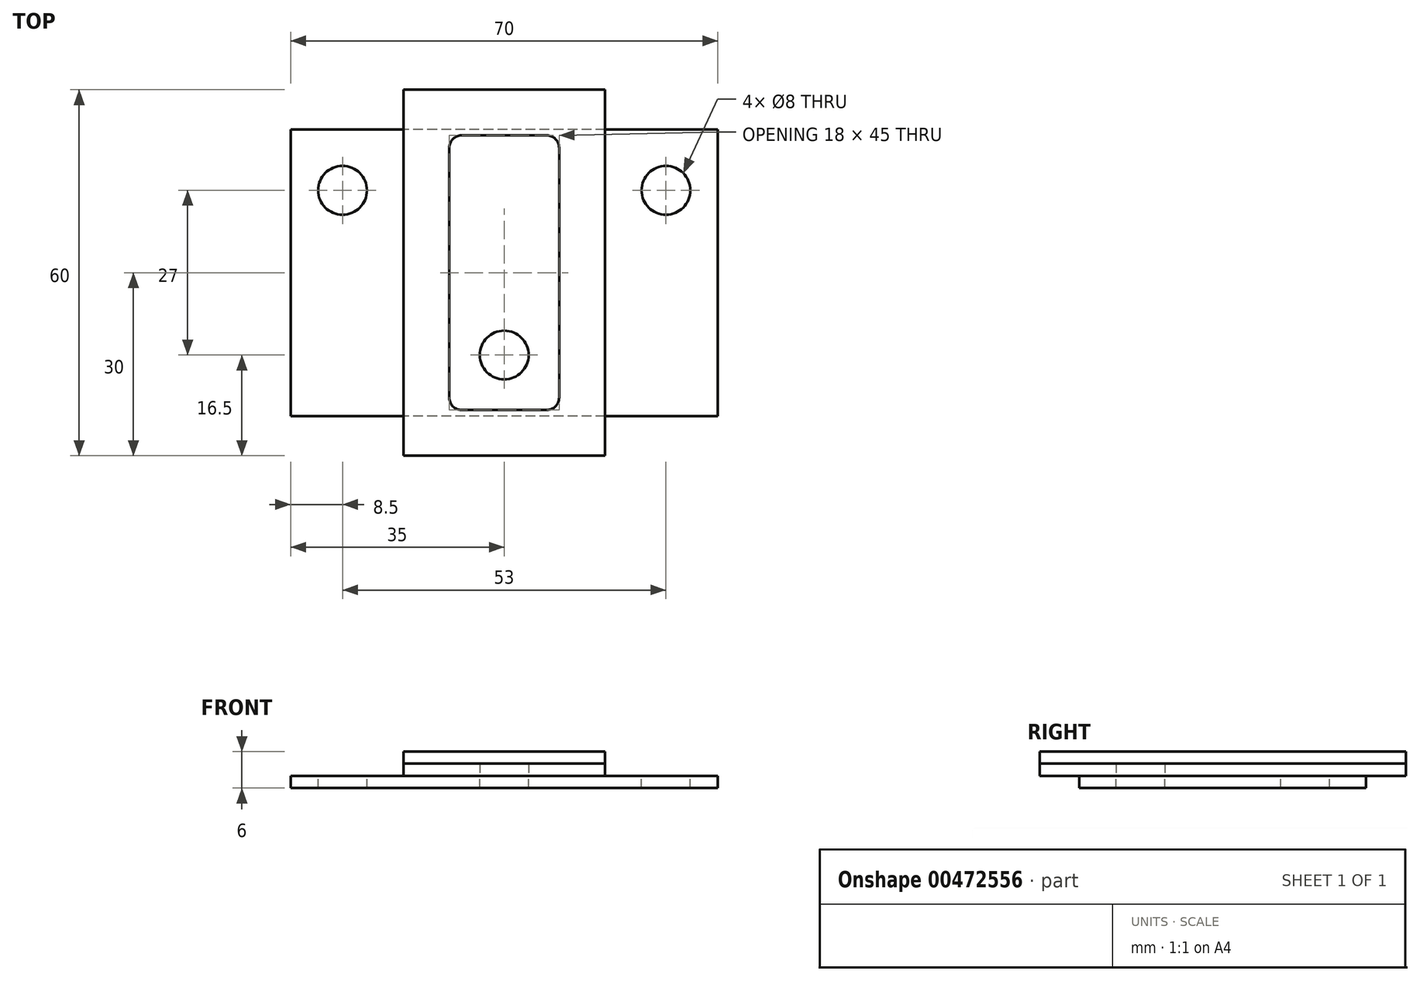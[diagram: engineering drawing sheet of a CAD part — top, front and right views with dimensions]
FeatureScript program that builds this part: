
annotation { "Feature Type Name" : "Feature", "Feature Type Description" : "" }
export const myFeature = defineFeature(function(context is Context, id is Id, definition is map)
    precondition{}
    {
        {
            var Q0;
            Q0=qCreatedBy(makeId("Top.planeOp"),FACE);
            var sketch = newSketch(context, id + "F0", { "sketchPlane" : qUnion([Q0])});
            skLineSegment(sketch, "E0.bottom", {"start": v(35, -23.5) * mm, "end": v(-35, -23.5) * mm});
            skLineSegment(sketch, "E0.top", {"start": v(35, 23.5) * mm, "end": v(-35, 23.5) * mm});
            skLineSegment(sketch, "E0.left", {"start": v(35, -23.5) * mm, "end": v(35, 23.5) * mm});
            skLineSegment(sketch, "E0.right", {"start": v(-35, -23.5) * mm, "end": v(-35, 23.5) * mm});
            skPoint(sketch, "E0.middle", {"position": v(0, 0) * mm});
            skCircle(sketch, "E1", {"center": v(-26.5, 13.5) * mm, "radius": 4 * mm});
            skCircle(sketch, "E2", {"center": v(26.5, 13.5) * mm, "radius": 4 * mm});
            skCircle(sketch, "E3", {"center": v(0, -13.5) * mm, "radius": 4 * mm});
            skSolve(sketch);
        }
        {
            var Q0;
            Q0=qCreatedBy(makeId("Top.planeOp"),FACE);
            var sketch = newSketch(context, id + "F1", { "sketchPlane" : qUnion([Q0])});
            skLineSegment(sketch, "E4.bottom", {"start": v(7, -22.5) * mm, "end": v(-7, -22.5) * mm});
            skLineSegment(sketch, "E4.top", {"start": v(7, 22.5) * mm, "end": v(-7, 22.5) * mm});
            skLineSegment(sketch, "E4.left", {"start": v(9, -20.5) * mm, "end": v(9, 20.5) * mm});
            skLineSegment(sketch, "E4.right", {"start": v(-9, -20.5) * mm, "end": v(-9, 20.5) * mm});
            skPoint(sketch, "E4.middle", {"position": v(0, 0) * mm});
            skPoint(sketch, "E5.visualSharp", {"position": v(9, 22.5) * mm});
            skArc(sketch, "E5.filletArc", {"start": v(9, 20.5) * mm, "mid": v(8.41, 21.91) * mm, "end": v(7, 22.5) * mm});
            skPoint(sketch, "E6.visualSharp", {"position": v(-9, 22.5) * mm});
            skArc(sketch, "E6.filletArc", {"start": v(-7, 22.5) * mm, "mid": v(-8.41, 21.91) * mm, "end": v(-9, 20.5) * mm});
            skPoint(sketch, "E7.visualSharp", {"position": v(9, -22.5) * mm});
            skArc(sketch, "E7.filletArc", {"start": v(7, -22.5) * mm, "mid": v(8.41, -21.91) * mm, "end": v(9, -20.5) * mm});
            skPoint(sketch, "E8.visualSharp", {"position": v(-9, -22.5) * mm});
            skArc(sketch, "E8.filletArc", {"start": v(-9, -20.5) * mm, "mid": v(-8.41, -21.91) * mm, "end": v(-7, -22.5) * mm});
            skLineSegment(sketch, "E9.bottom", {"start": v(16.5, -30) * mm, "end": v(-16.5, -30) * mm});
            skLineSegment(sketch, "E9.top", {"start": v(16.5, 30) * mm, "end": v(-16.5, 30) * mm});
            skLineSegment(sketch, "E9.left", {"start": v(16.5, -30) * mm, "end": v(16.5, 30) * mm});
            skLineSegment(sketch, "E9.right", {"start": v(-16.5, -30) * mm, "end": v(-16.5, 30) * mm});
            skSolve(sketch);
        }
        {
            var Q0;
            Q0=makeQuery(id+"F0.imprint","IMPRINT",FACE,{"disambiguationData":[TD([[makeQuery(id+"F0.imprint","IMPRINT",EDGE,{"derivedFrom":sQuery(id+"F0.wireOp",EDGE,"E0.bottom")}),-1.0]])]});
            extrude(context, id + "F2", {"entities" : qUnion([Q0]), "oppositeDirection" : true, "depth" : 2 * mm, "offsetDistance" : 25 * mm});
        }
        {
            var Q0;
            Q0=qCreatedBy(makeId("Top.planeOp"),FACE);
            var sketch = newSketch(context, id + "F3", { "sketchPlane" : qUnion([Q0])});
            skLineSegment(sketch, "E10.bottom", {"start": v(16.5, -30) * mm, "end": v(-16.5, -30) * mm});
            skLineSegment(sketch, "E10.top", {"start": v(16.5, 30) * mm, "end": v(-16.5, 30) * mm});
            skLineSegment(sketch, "E10.left", {"start": v(16.5, -30) * mm, "end": v(16.5, 30) * mm});
            skLineSegment(sketch, "E10.right", {"start": v(-16.5, -30) * mm, "end": v(-16.5, 30) * mm});
            skPoint(sketch, "E10.middle", {"position": v(0, 0) * mm});
            skCircle(sketch, "E11", {"center": v(0, -13.5) * mm, "radius": 4 * mm});
            skSolve(sketch);
        }
        {
            var Q0;
            Q0=makeQuery(id+"F3.imprint","IMPRINT",FACE,{"disambiguationData":[TD([[makeQuery(id+"F3.imprint","IMPRINT",EDGE,{"derivedFrom":sQuery(id+"F3.wireOp",EDGE,"E10.bottom")}),-1.0]])]});
            extrude(context, id + "F4", {"entities" : qUnion([Q0]), "depth" : 2 * mm, "offsetDistance" : 25 * mm});
        }
        {
            var Q0;
            Q0 = qSketchRegion(id + "F1", true);
            extrude(context, id + "F5", {"entities" : qUnion([Q0]), "depth" : 4 * mm, "offsetDistance" : 25 * mm});
        }
    });
